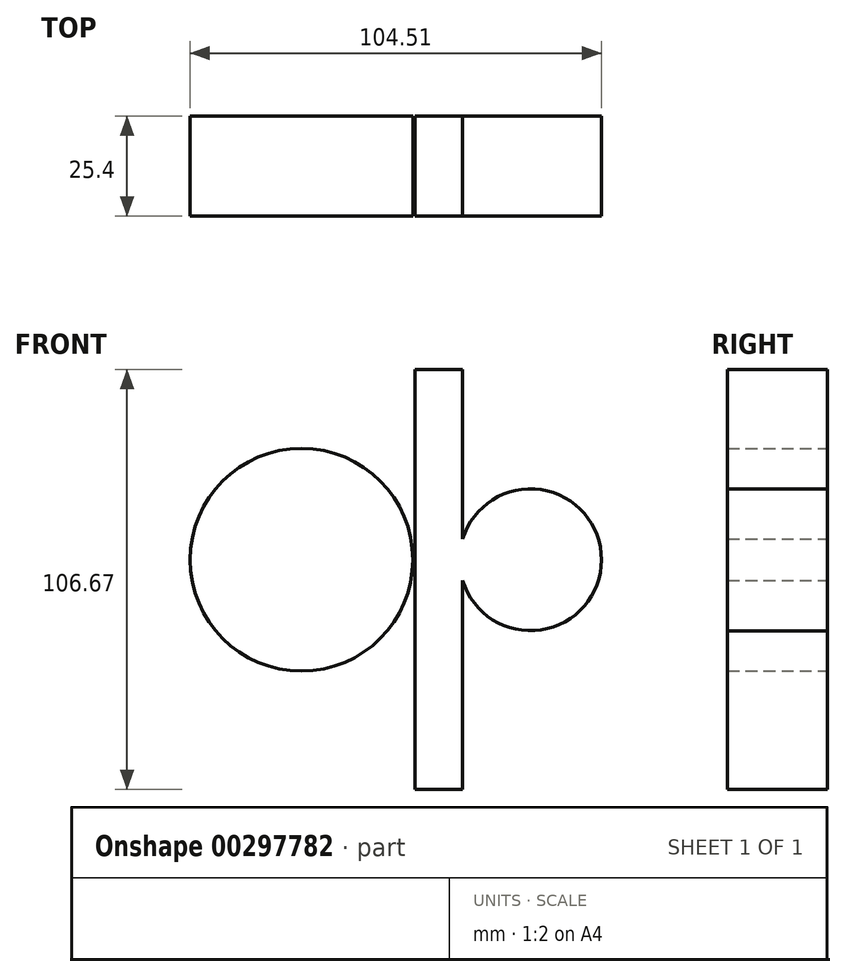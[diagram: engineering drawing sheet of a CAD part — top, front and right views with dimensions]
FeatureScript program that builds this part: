
annotation { "Feature Type Name" : "Feature", "Feature Type Description" : "" }
export const myFeature = defineFeature(function(context is Context, id is Id, definition is map)
    precondition{}
    {
        {
            var Q0;
            Q0=qCreatedBy(makeId("Front.planeOp"),FACE);
            var sketch = newSketch(context, id + "F0", { "sketchPlane" : qUnion([Q0])});
            skLineSegment(sketch, "E0.bottom", {"start": v(0, 48.33) * mm, "end": v(12.08, 48.33) * mm});
            skLineSegment(sketch, "E0.top", {"start": v(0, -58.34) * mm, "end": v(12.08, -58.34) * mm});
            skLineSegment(sketch, "E0.left", {"start": v(0, 48.33) * mm, "end": v(0, -58.34) * mm});
            skLineSegment(sketch, "E0.right", {"start": v(12.08, 48.33) * mm, "end": v(12.08, -58.34) * mm});
            skCircle(sketch, "E1", {"center": v(29.32, 0) * mm, "radius": 18.02 * mm});
            skCircle(sketch, "E2", {"center": v(-28.88, 0) * mm, "radius": 28.3 * mm});
            skSolve(sketch);
        }
        {
            var Q0;
            Q0 = qSketchRegion(id + "F0", true);
            extrude(context, id + "F1", {"entities" : qUnion([Q0]), "depth" : 25.4 * mm});
        }
    });
